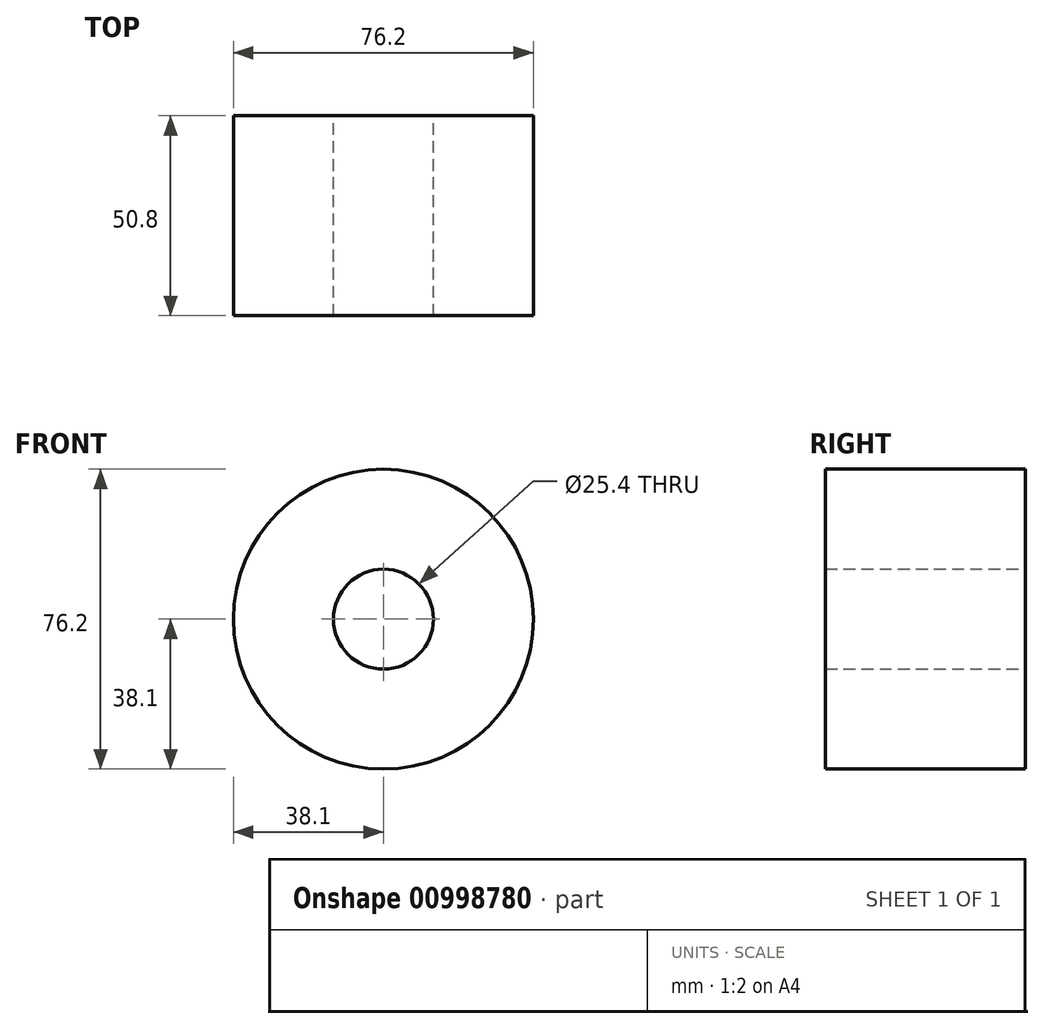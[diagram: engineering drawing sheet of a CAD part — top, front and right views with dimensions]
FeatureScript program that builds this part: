
annotation { "Feature Type Name" : "Feature", "Feature Type Description" : "" }
export const myFeature = defineFeature(function(context is Context, id is Id, definition is map)
    precondition{}
    {
        {
            var Q0;
            Q0=qCreatedBy(makeId("Front.planeOp"),FACE);
            var sketch = newSketch(context, id + "F0", { "sketchPlane" : qUnion([Q0])});
            skCircle(sketch, "E0", {"center": v(0, 0) * mm, "radius": 12.7 * mm});
            skCircle(sketch, "E1", {"center": v(0, 0) * mm, "radius": 38.1 * mm});
            skSolve(sketch);
        }
        {
            var Q0;
            Q0=makeQuery(id+"F0.imprint","IMPRINT",FACE,{"disambiguationData":[TD([[makeQuery(id+"F0.imprint","IMPRINT",EDGE,{"derivedFrom":sQuery(id+"F0.wireOp",EDGE,"E0")}),-1.0]])]});
            extrude(context, id + "F1", {"entities" : qUnion([Q0]), "depth" : 50.8 * mm, "offsetDistance" : 25.4 * mm});
        }
    });
